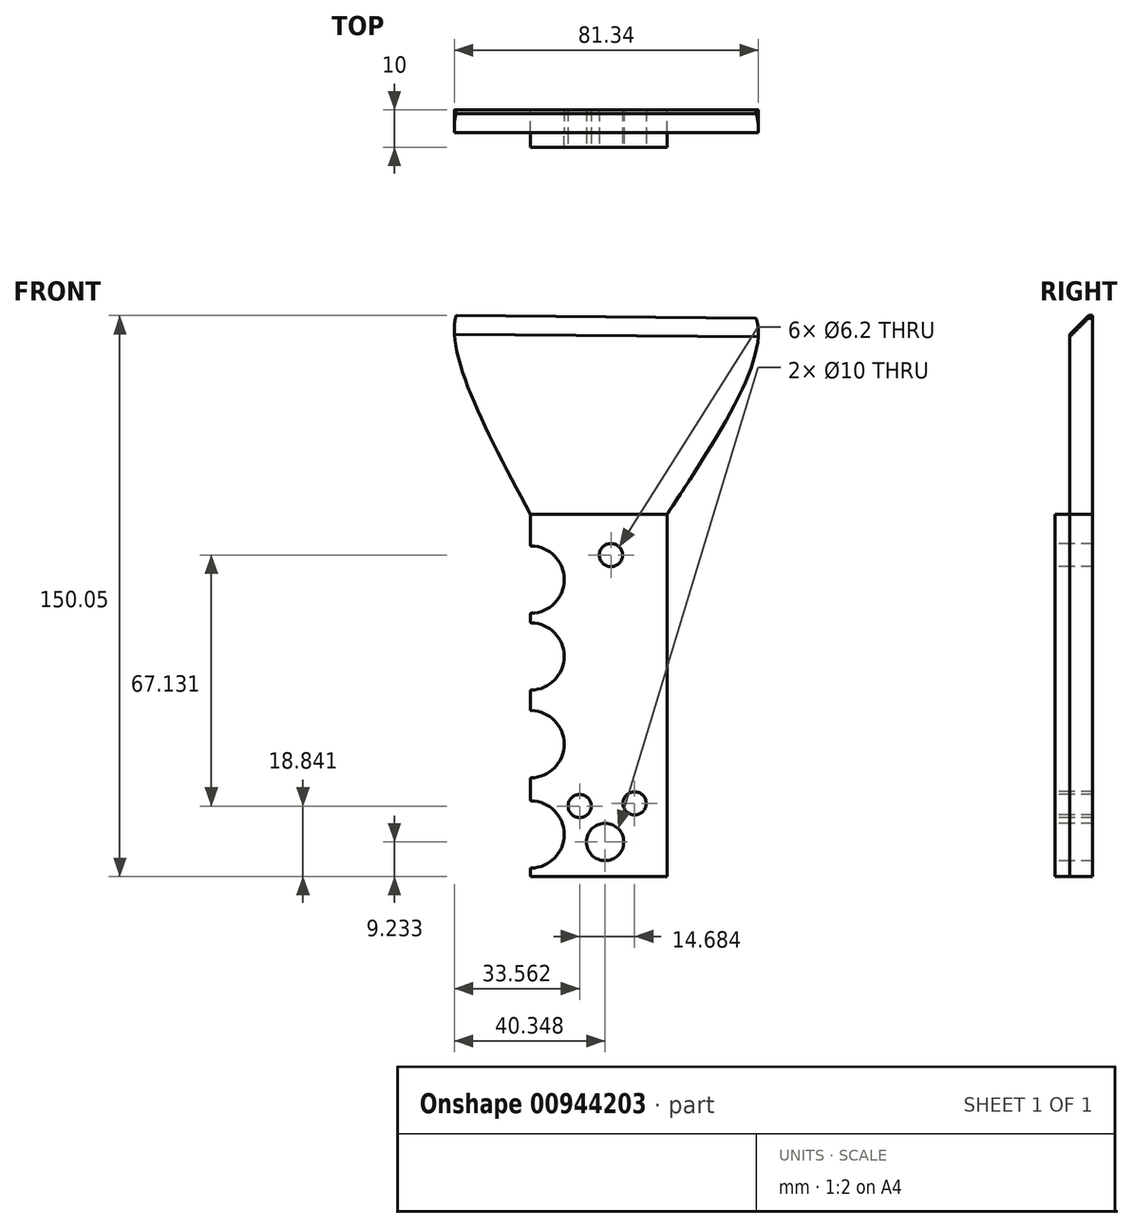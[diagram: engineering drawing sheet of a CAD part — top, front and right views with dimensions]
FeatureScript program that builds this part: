
annotation { "Feature Type Name" : "Feature", "Feature Type Description" : "" }
export const myFeature = defineFeature(function(context is Context, id is Id, definition is map)
    precondition{}
    {
        {
            var Q0;
            Q0=qCreatedBy(makeId("Front.planeOp"),FACE);
            var sketch = newSketch(context, id + "F0", { "sketchPlane" : qUnion([Q0])});
            skLineSegment(sketch, "E0.bottom", {"start": v(-32.88, 118.1) * mm, "end": v(47.12, 118.1) * mm});
            skLineSegment(sketch, "E0.top", {"start": v(-32.88, -31.9) * mm, "end": v(47.12, -31.9) * mm});
            skLineSegment(sketch, "E0.left", {"start": v(-32.88, 118.1) * mm, "end": v(-32.88, -31.9) * mm});
            skLineSegment(sketch, "E0.right", {"start": v(47.12, 118.1) * mm, "end": v(47.12, -31.9) * mm});
            skSolve(sketch);
        }
        {
            var Q0;
            Q0=makeQuery(id+"F0.imprint","IMPRINT",FACE,{"disambiguationData":[TD([[makeQuery(id+"F0.imprint","IMPRINT",EDGE,{"derivedFrom":sQuery(id+"F0.wireOp",EDGE,"E0.bottom")}),-1.0]])]});
            var sketch = newSketch(context, id + "F1", { "sketchPlane" : qUnion([Q0])});
            skLineSegment(sketch, "E1", {"start": v(-32.95, 65.56) * mm, "end": v(47.62, 65.56) * mm});
            skLineSegment(sketch, "E2", {"start": v(47.62, 65.56) * mm, "end": v(23.81, 65.56) * mm});
            skLineSegment(sketch, "E3", {"start": v(23.81, 65.56) * mm, "end": v(23.81, -31.32) * mm});
            skLineSegment(sketch, "E4", {"start": v(23.81, -31.32) * mm, "end": v(-12.72, -31.32) * mm});
            skLineSegment(sketch, "E5", {"start": v(-12.72, -31.32) * mm, "end": v(-12.72, 65.56) * mm});
            skFitSpline(sketch, "E6", {"points": [v(-12.72, 65.56) * mm, v(-32.62, 118.73) * mm, v(-18.6, 129.17) * mm], "startDerivative": vector(-53.53, 99.86) * mm, "endDerivative": vector(51.84, 19.71) * mm});
            skFitSpline(sketch, "E7", {"points": [v(23.81, 65.56) * mm, v(47.62, 118.08) * mm, v(23.81, 131.13) * mm], "startDerivative": vector(69.41, 105.31) * mm, "endDerivative": vector(-78.6, 20.57) * mm});
            skLineSegment(sketch, "E8", {"start": v(-32.62, 118.73) * mm, "end": v(47.62, 118.08) * mm});
            skSolve(sketch);
        }
        {
            var Q0;
            Q0 = qSketchRegion(id + "F1", true);
            extrude(context, id + "F2", {"entities" : qUnion([Q0]), "depth" : 6 * mm, "offsetDistance" : 25 * mm});
        }
        {
            var Q0;
            Q0=makeQuery(id+"F2.opExtrude","CAP_FACE",FACE,{"disambiguationData":[OSD([sQuery(id+"F1.wireOp",EDGE,"E3"),sQuery(id+"F1.wireOp",EDGE,"E4"),sQuery(id+"F1.wireOp",EDGE,"E5"),sQuery(id+"F1.wireOp",EDGE,"E6"),sQuery(id+"F1.wireOp",EDGE,"E7"),sQuery(id+"F1.wireOp",EDGE,"E8")])],"isStart":false});
            var sketch = newSketch(context, id + "F3", { "sketchPlane" : qUnion([Q0])});
            skLineSegment(sketch, "E9", {"start": v(-12.72, 65.56) * mm, "end": v(23.81, 65.56) * mm});
            skCircle(sketch, "E10", {"center": v(-12.72, 48.1) * mm, "radius": 9 * mm});
            skCircle(sketch, "E11", {"center": v(-12.72, 27.55) * mm, "radius": 9 * mm});
            skCircle(sketch, "E12", {"center": v(-12.72, 4.06) * mm, "radius": 9 * mm});
            skCircle(sketch, "E13", {"center": v(-12.72, -20.08) * mm, "radius": 9 * mm});
            skSolve(sketch);
        }
        {
            var Q0;
            {var subQ9=sQuery(id+"F3.wireOp",EDGE,"E9");Q0=makeQuery(id+"F3.imprint","IMPRINT",FACE,{"disambiguationData":[TD([[makeQuery(id+"F3.imprint","IMPRINT",EDGE,{"derivedFrom":subQ9}),-1.0]])]});}
            extrude(context, id + "F4", {"entities" : qUnion([Q0]), "depth" : 4 * mm, "offsetDistance" : 25 * mm});
        }
        {
            var Q0;
            Q0 = qSketchRegion(id + "F3", true);
            extrude(context, id + "F5", {"entities" : qUnion([Q0]), "operationType" : NewBodyOperationType.REMOVE, "oppositeDirection" : true, "depth" : 25 * mm, "offsetDistance" : 25 * mm});
        }
        {
            var Q0;
            Q0=makeQuery(id+"F4.opExtrude","CAP_FACE",FACE,{"disambiguationData":[OSD([sQuery(id+"F1.wireOp",EDGE,"E3"),sQuery(id+"F1.wireOp",EDGE,"E4"),sQuery(id+"F1.wireOp",EDGE,"E5"),sQuery(id+"F3.wireOp",EDGE,"E9"),sQuery(id+"F3.wireOp",EDGE,"E10"),sQuery(id+"F3.wireOp",EDGE,"E11"),sQuery(id+"F3.wireOp",EDGE,"E12"),sQuery(id+"F3.wireOp",EDGE,"E13")])],"isStart":false});
            var sketch = newSketch(context, id + "F6", { "sketchPlane" : qUnion([Q0])});
            skCircle(sketch, "E14", {"center": v(0.44, -12.48) * mm, "radius": 3.1 * mm});
            skCircle(sketch, "E15", {"center": v(15.13, -11.76) * mm, "radius": 3.1 * mm});
            skCircle(sketch, "E16", {"center": v(8.82, 54.65) * mm, "radius": 3.1 * mm});
            skCircle(sketch, "E17", {"center": v(7.23, -22.09) * mm, "radius": 5 * mm});
            skSolve(sketch);
        }
        {
            var Q0;
            Q0 = qSketchRegion(id + "F6", true);
            extrude(context, id + "F7", {"entities" : qUnion([Q0]), "operationType" : NewBodyOperationType.REMOVE, "oppositeDirection" : true, "depth" : 35.6 * mm, "offsetDistance" : 25 * mm});
        }
        {
            var Q0;
            Q0=makeQuery(id+"F2.opExtrude","CAP_EDGE",EDGE,{"disambiguationData":[OSD([sQuery(id+"F1.wireOp",EDGE,"E8")])],"isStart":false});
            chamfer(context, id + "F8", {"entities" : qUnion([Q0]), "width" : 5 * mm, "tangentPropagation" : true});
        }
        {
            var Q0;
            Q0=makeQuery(id+"F5.boolean.opBoolean","INTERSECT",EDGE,{"disambiguationData":[OD(0.0)],"derivedFrom":[makeQuery(id+"F2.opExtrude","SWEPT_FACE",FACE,{"disambiguationData":[OSD([sQuery(id+"F1.wireOp",EDGE,"E5")])]}),makeQuery(id+"F5.opExtrude","SWEPT_FACE",FACE,{"disambiguationData":[OSD([sQuery(id+"F3.wireOp",EDGE,"E10")])]})]});
            var Q1;
            {var subQ0=sQuery(id+"F3.wireOp",EDGE,"E10");var subQ1=sQuery(id+"F1.wireOp",EDGE,"E5");Q1=makeQuery(id+"F4.opExtrude","SWEPT_EDGE",EDGE,{"disambiguationData":[OSD([subQ1,subQ0]),TDD([makeQuery(id+"F3.imprint","INTERSECT",VERTEX,{"disambiguationData":[OD(0.0)],"derivedFrom":[makeQuery(id+"F2.opExtrude","CAP_EDGE",EDGE,{"disambiguationData":[OSD([subQ1])],"isStart":false}),subQ0]})])]});}
            var Q2;
            {var subQ0=sQuery(id+"F3.wireOp",EDGE,"E11");var subQ1=sQuery(id+"F1.wireOp",EDGE,"E5");Q2=makeQuery(id+"F4.opExtrude","SWEPT_EDGE",EDGE,{"disambiguationData":[OSD([subQ1,subQ0]),TDD([makeQuery(id+"F3.imprint","INTERSECT",VERTEX,{"disambiguationData":[OD(0.0)],"derivedFrom":[makeQuery(id+"F2.opExtrude","CAP_EDGE",EDGE,{"disambiguationData":[OSD([subQ1])],"isStart":false}),subQ0]})])]});}
            var Q3;
            Q3=makeQuery(id+"F5.boolean.opBoolean","INTERSECT",EDGE,{"disambiguationData":[OD(0.0)],"derivedFrom":[makeQuery(id+"F2.opExtrude","SWEPT_FACE",FACE,{"disambiguationData":[OSD([sQuery(id+"F1.wireOp",EDGE,"E5")])]}),makeQuery(id+"F5.opExtrude","SWEPT_FACE",FACE,{"disambiguationData":[OSD([sQuery(id+"F3.wireOp",EDGE,"E11")])]})]});
            var Q4;
            {var subQ0=sQuery(id+"F3.wireOp",EDGE,"E10");var subQ1=sQuery(id+"F1.wireOp",EDGE,"E5");Q4=makeQuery(id+"F4.opExtrude","SWEPT_EDGE",EDGE,{"disambiguationData":[OSD([subQ1,subQ0]),TDD([makeQuery(id+"F3.imprint","INTERSECT",VERTEX,{"disambiguationData":[OD(1.0)],"derivedFrom":[makeQuery(id+"F2.opExtrude","CAP_EDGE",EDGE,{"disambiguationData":[OSD([subQ1])],"isStart":false}),subQ0]})])]});}
            var Q5;
            Q5=makeQuery(id+"F5.boolean.opBoolean","INTERSECT",EDGE,{"disambiguationData":[OD(1.0)],"derivedFrom":[makeQuery(id+"F2.opExtrude","SWEPT_FACE",FACE,{"disambiguationData":[OSD([sQuery(id+"F1.wireOp",EDGE,"E5")])]}),makeQuery(id+"F5.opExtrude","SWEPT_FACE",FACE,{"disambiguationData":[OSD([sQuery(id+"F3.wireOp",EDGE,"E10")])]})]});
            var Q6;
            {var subQ0=sQuery(id+"F3.wireOp",EDGE,"E11");var subQ1=sQuery(id+"F1.wireOp",EDGE,"E5");Q6=makeQuery(id+"F4.opExtrude","SWEPT_EDGE",EDGE,{"disambiguationData":[OSD([subQ1,subQ0]),TDD([makeQuery(id+"F3.imprint","INTERSECT",VERTEX,{"disambiguationData":[OD(1.0)],"derivedFrom":[makeQuery(id+"F2.opExtrude","CAP_EDGE",EDGE,{"disambiguationData":[OSD([subQ1])],"isStart":false}),subQ0]})])]});}
            var Q7;
            Q7=makeQuery(id+"F5.boolean.opBoolean","INTERSECT",EDGE,{"disambiguationData":[OD(0.0)],"derivedFrom":[makeQuery(id+"F2.opExtrude","SWEPT_FACE",FACE,{"disambiguationData":[OSD([sQuery(id+"F1.wireOp",EDGE,"E5")])]}),makeQuery(id+"F5.opExtrude","SWEPT_FACE",FACE,{"disambiguationData":[OSD([sQuery(id+"F3.wireOp",EDGE,"E12")])]})]});
            var Q8;
            {var subQ0=sQuery(id+"F3.wireOp",EDGE,"E12");var subQ1=sQuery(id+"F1.wireOp",EDGE,"E5");Q8=makeQuery(id+"F4.opExtrude","SWEPT_EDGE",EDGE,{"disambiguationData":[OSD([subQ1,subQ0]),TDD([makeQuery(id+"F3.imprint","INTERSECT",VERTEX,{"disambiguationData":[OD(1.0)],"derivedFrom":[makeQuery(id+"F2.opExtrude","CAP_EDGE",EDGE,{"disambiguationData":[OSD([subQ1])],"isStart":false}),subQ0]})])]});}
            var Q9;
            Q9=makeQuery(id+"F5.boolean.opBoolean","INTERSECT",EDGE,{"disambiguationData":[OD(1.0)],"derivedFrom":[makeQuery(id+"F2.opExtrude","SWEPT_FACE",FACE,{"disambiguationData":[OSD([sQuery(id+"F1.wireOp",EDGE,"E5")])]}),makeQuery(id+"F5.opExtrude","SWEPT_FACE",FACE,{"disambiguationData":[OSD([sQuery(id+"F3.wireOp",EDGE,"E11")])]})]});
            var Q10;
            Q10=makeQuery(id+"F5.boolean.opBoolean","INTERSECT",EDGE,{"disambiguationData":[OD(1.0)],"derivedFrom":[makeQuery(id+"F2.opExtrude","SWEPT_FACE",FACE,{"disambiguationData":[OSD([sQuery(id+"F1.wireOp",EDGE,"E5")])]}),makeQuery(id+"F5.opExtrude","SWEPT_FACE",FACE,{"disambiguationData":[OSD([sQuery(id+"F3.wireOp",EDGE,"E12")])]})]});
            var Q11;
            {var subQ0=sQuery(id+"F3.wireOp",EDGE,"E12");var subQ1=sQuery(id+"F1.wireOp",EDGE,"E5");Q11=makeQuery(id+"F4.opExtrude","SWEPT_EDGE",EDGE,{"disambiguationData":[OSD([subQ1,subQ0]),TDD([makeQuery(id+"F3.imprint","INTERSECT",VERTEX,{"disambiguationData":[OD(0.0)],"derivedFrom":[makeQuery(id+"F2.opExtrude","CAP_EDGE",EDGE,{"disambiguationData":[OSD([subQ1])],"isStart":false}),subQ0]})])]});}
            var Q12;
            Q12=makeQuery(id+"F5.boolean.opBoolean","INTERSECT",EDGE,{"disambiguationData":[OD(1.0)],"derivedFrom":[makeQuery(id+"F2.opExtrude","SWEPT_FACE",FACE,{"disambiguationData":[OSD([sQuery(id+"F1.wireOp",EDGE,"E5")])]}),makeQuery(id+"F5.opExtrude","SWEPT_FACE",FACE,{"disambiguationData":[OSD([sQuery(id+"F3.wireOp",EDGE,"E13")])]})]});
            var Q13;
            Q13=makeQuery(id+"F5.boolean.opBoolean","INTERSECT",EDGE,{"disambiguationData":[OD(0.0)],"derivedFrom":[makeQuery(id+"F2.opExtrude","SWEPT_FACE",FACE,{"disambiguationData":[OSD([sQuery(id+"F1.wireOp",EDGE,"E5")])]}),makeQuery(id+"F5.opExtrude","SWEPT_FACE",FACE,{"disambiguationData":[OSD([sQuery(id+"F3.wireOp",EDGE,"E13")])]})]});
            var Q14;
            {var subQ0=sQuery(id+"F3.wireOp",EDGE,"E13");var subQ1=sQuery(id+"F1.wireOp",EDGE,"E5");Q14=makeQuery(id+"F4.opExtrude","SWEPT_EDGE",EDGE,{"disambiguationData":[OSD([subQ1,subQ0]),TDD([makeQuery(id+"F3.imprint","INTERSECT",VERTEX,{"disambiguationData":[OD(0.0)],"derivedFrom":[makeQuery(id+"F2.opExtrude","CAP_EDGE",EDGE,{"disambiguationData":[OSD([subQ1])],"isStart":false}),subQ0]})])]});}
            var Q15;
            Q15=makeQuery(id+"F2.opExtrude","SWEPT_EDGE",EDGE,{"disambiguationData":[OSD([sQuery(id+"F1.wireOp",EDGE,"E4"),sQuery(id+"F1.wireOp",EDGE,"E5")])]});
            var Q16;
            Q16=makeQuery(id+"F4.opExtrude","SWEPT_EDGE",EDGE,{"disambiguationData":[OSD([sQuery(id+"F1.wireOp",EDGE,"E4"),sQuery(id+"F1.wireOp",EDGE,"E5")])]});
            var Q17;
            {var subQ0=sQuery(id+"F3.wireOp",EDGE,"E13");var subQ1=sQuery(id+"F1.wireOp",EDGE,"E5");Q17=makeQuery(id+"F4.opExtrude","SWEPT_EDGE",EDGE,{"disambiguationData":[OSD([subQ1,subQ0]),TDD([makeQuery(id+"F3.imprint","INTERSECT",VERTEX,{"disambiguationData":[OD(1.0)],"derivedFrom":[makeQuery(id+"F2.opExtrude","CAP_EDGE",EDGE,{"disambiguationData":[OSD([subQ1])],"isStart":false}),subQ0]})])]});}
            fillet(context, id + "F9", {"entities" : qUnion([Q0, Q1, Q2, Q3, Q4, Q5, Q6, Q7, Q8, Q9, Q10, Q11, Q12, Q13, Q14, Q15, Q16, Q17]), "radius" : 0.24 * mm, "tangentPropagation" : true, "allowEdgeOverflow" : false});
        }
    });
